# Revit family: Plumbing Fixture-Grease_Interseptor_Mifab_MI-HEL
name_source: partatom
category: Plumbing Fixtures
revit_build: Autodesk Revit Structure 2013 (Build: 20120221_2030(x64)
units: mm (PartAtom-declared; Revit-internal decimal feet)

## types (6) — shared parameters
Assembly Code = D2090300
C = 12 "
D = 36 "
Description = Heliport Fual Spill Interceptors
E = 48 "
F = 6 "
Interceptor Material = Acid Resistant Epoxy Coated Green
Manufacturer = MIFAB
Standard Inlet And Outlet Radii = 3 "
URL = www.mifab.com
zero-valued in all types: Default Elevation, WFU

## per-type parameters (varying)
| type | A | B | Fuel Retention Capacity |
| MI-HEL-1 | 90 " | 36 " | 35 Gallons |
| MI-HEL-2 | 126 " | 48 " | 65 Gallons |
| MI-HEL-3 | 132 " | 63 " | 90 Gallons |
| MI-HEL-4 | 192 " | 92 " | 195 Gallons |
| MI-HEL-5 | 213 " | 96 " | 220 Gallons |
| MI-HEL-6 | 240 " | 96 " | 250 Gallons |

note: column(s) folded — value = type name in every type: Model

## geometry (parser evidence)
native form markers: Blend x4, Sweep x1
no freeform markers — native parametric forms only
